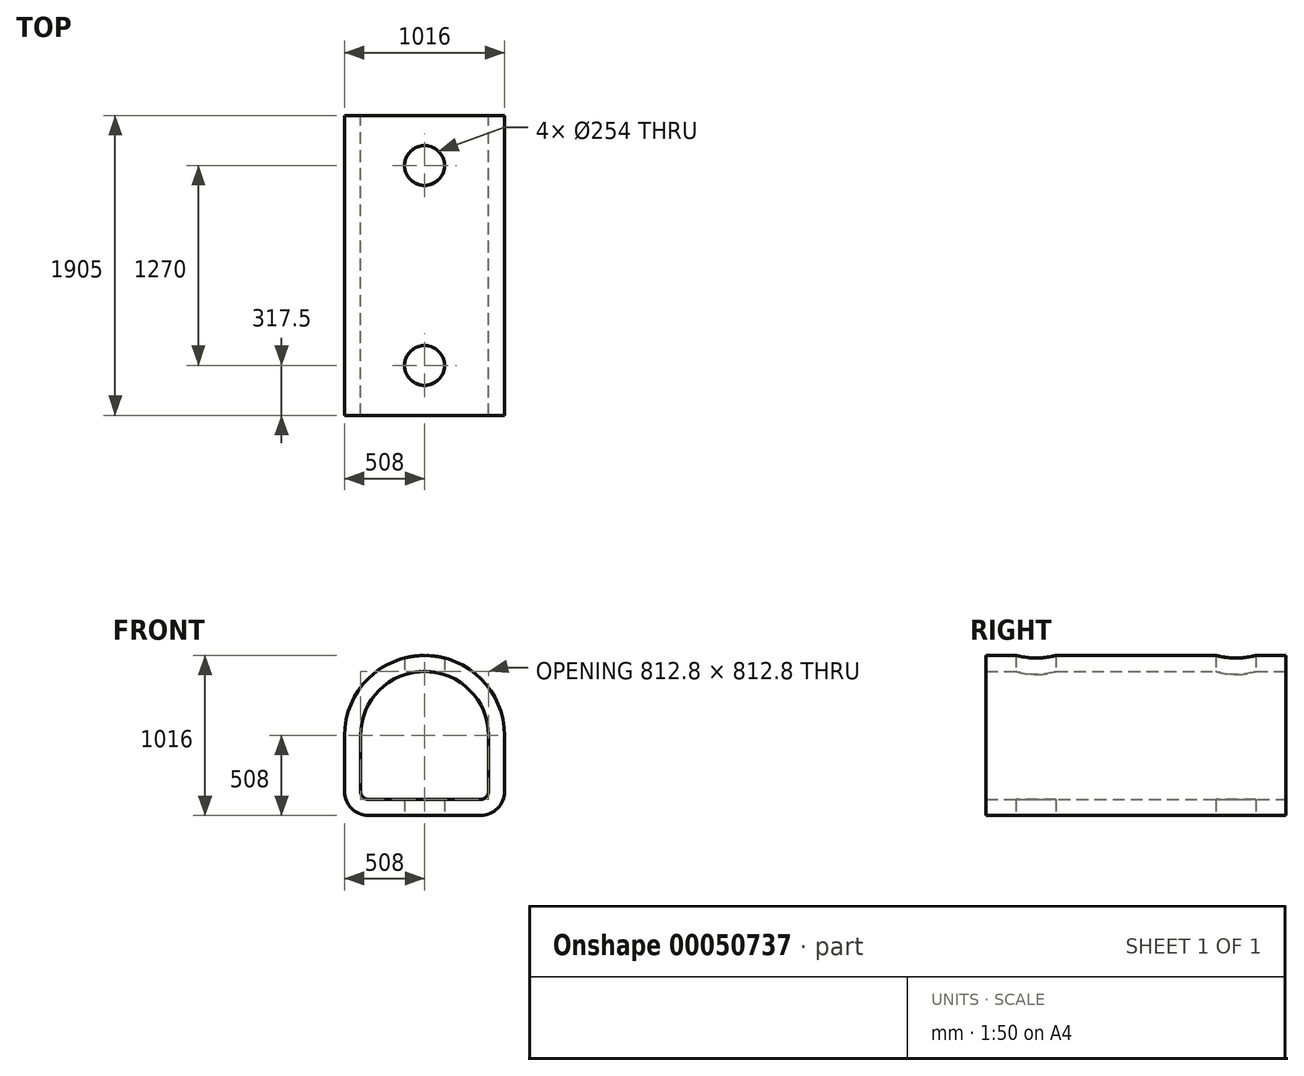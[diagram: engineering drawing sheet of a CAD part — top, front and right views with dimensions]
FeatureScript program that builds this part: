
annotation { "Feature Type Name" : "Feature", "Feature Type Description" : "" }
export const myFeature = defineFeature(function(context is Context, id is Id, definition is map)
    precondition{}
    {
        {
            var Q0;
            Q0=qCreatedBy(makeId("Front.planeOp"),FACE);
            var sketch = newSketch(context, id + "F0", { "sketchPlane" : qUnion([Q0])});
            skArc(sketch, "E0", {"start": v(508, 508) * mm, "mid": v(0, 1016) * mm, "end": v(-508, 508) * mm});
            skLineSegment(sketch, "E1", {"start": v(-659.72, 508) * mm, "end": v(725.41, 508) * mm, "construction": true});
            skLineSegment(sketch, "E2", {"start": v(0, 1367.6) * mm, "end": v(0, -81.1) * mm, "construction": true});
            skLineSegment(sketch, "E3", {"start": v(-508, 508) * mm, "end": v(-508, 152.4) * mm});
            skLineSegment(sketch, "E4", {"start": v(-355.6, 0) * mm, "end": v(0, 0) * mm});
            skLineSegment(sketch, "E5.MirrorCS", {"start": v(508, 508) * mm, "end": v(508, 152.4) * mm});
            skLineSegment(sketch, "E6.MirrorCS", {"start": v(355.6, 0) * mm, "end": v(0, 0) * mm});
            skPoint(sketch, "E7.visualSharp", {"position": v(-508, 0) * mm});
            skArc(sketch, "E7.filletArc", {"start": v(-508, 152.4) * mm, "mid": v(-463.36, 44.64) * mm, "end": v(-355.6, 0) * mm});
            skPoint(sketch, "E8.visualSharp", {"position": v(508, 0) * mm});
            skArc(sketch, "E8.filletArc", {"start": v(355.6, 0) * mm, "mid": v(463.36, 44.64) * mm, "end": v(508, 152.4) * mm});
            skLineSegment(sketch, "E9.0", {"start": v(406.4, 508) * mm, "end": v(406.4, 152.4) * mm});
            skArc(sketch, "E9.1", {"start": v(355.6, 101.6) * mm, "mid": v(391.52, 116.48) * mm, "end": v(406.4, 152.4) * mm});
            skLineSegment(sketch, "E9.2", {"start": v(-406.4, 508) * mm, "end": v(-406.4, 152.4) * mm});
            skArc(sketch, "E9.3", {"start": v(-406.4, 152.4) * mm, "mid": v(-391.52, 116.48) * mm, "end": v(-355.6, 101.6) * mm});
            skLineSegment(sketch, "E9.4", {"start": v(-355.6, 101.6) * mm, "end": v(0, 101.6) * mm});
            skArc(sketch, "E9.5", {"start": v(406.4, 508) * mm, "mid": v(0, 914.4) * mm, "end": v(-406.4, 508) * mm});
            skLineSegment(sketch, "E9.6", {"start": v(355.6, 101.6) * mm, "end": v(0, 101.6) * mm});
            skSolve(sketch);
        }
        {
            var Q0;
            Q0=makeQuery(id+"F0.imprint","IMPRINT",FACE,{"disambiguationData":[TD([[makeQuery(id+"F0.imprint","IMPRINT",EDGE,{"derivedFrom":sQuery(id+"F0.wireOp",EDGE,"E0")}),1.0]])]});
            extrude(context, id + "F1", {"entities" : qUnion([Q0]), "depth" : 1905 * mm});
        }
        {
            var Q0;
            Q0=makeQuery(id+"F1.opExtrude","SWEPT_FACE",FACE,{"disambiguationData":[OSD([sQuery(id+"F0.wireOp",EDGE,"E4"),sQuery(id+"F0.wireOp",EDGE,"E6.MirrorCS")])]});
            var sketch = newSketch(context, id + "F2", { "sketchPlane" : qUnion([Q0])});
            skLineSegment(sketch, "E10", {"start": v(0, 1905) * mm, "end": v(0, 0) * mm, "construction": true});
            skCircle(sketch, "E11", {"center": v(0, 952.5) * mm, "radius": 635 * mm, "construction": true});
            skCircle(sketch, "E12", {"center": v(0, 1587.5) * mm, "radius": 127 * mm});
            skCircle(sketch, "E13", {"center": v(0, 317.5) * mm, "radius": 127 * mm});
            skSolve(sketch);
        }
        {
            var Q0;
            Q0=makeQuery(id+"F2.imprint","IMPRINT",FACE,{"disambiguationData":[TD([[makeQuery(id+"F2.imprint","IMPRINT",EDGE,{"derivedFrom":sQuery(id+"F2.wireOp",EDGE,"E12")}),1.0]])]});
            var Q1;
            Q1=makeQuery(id+"F2.imprint","IMPRINT",FACE,{"disambiguationData":[TD([[makeQuery(id+"F2.imprint","IMPRINT",EDGE,{"derivedFrom":sQuery(id+"F2.wireOp",EDGE,"E13")}),1.0]])]});
            extrude(context, id + "F3", {"entities" : qUnion([Q0, Q1]), "operationType" : NewBodyOperationType.REMOVE, "endBound" : BoundingType.THROUGH_ALL, "oppositeDirection" : true, "depth" : 25.4 * mm});
        }
    });
